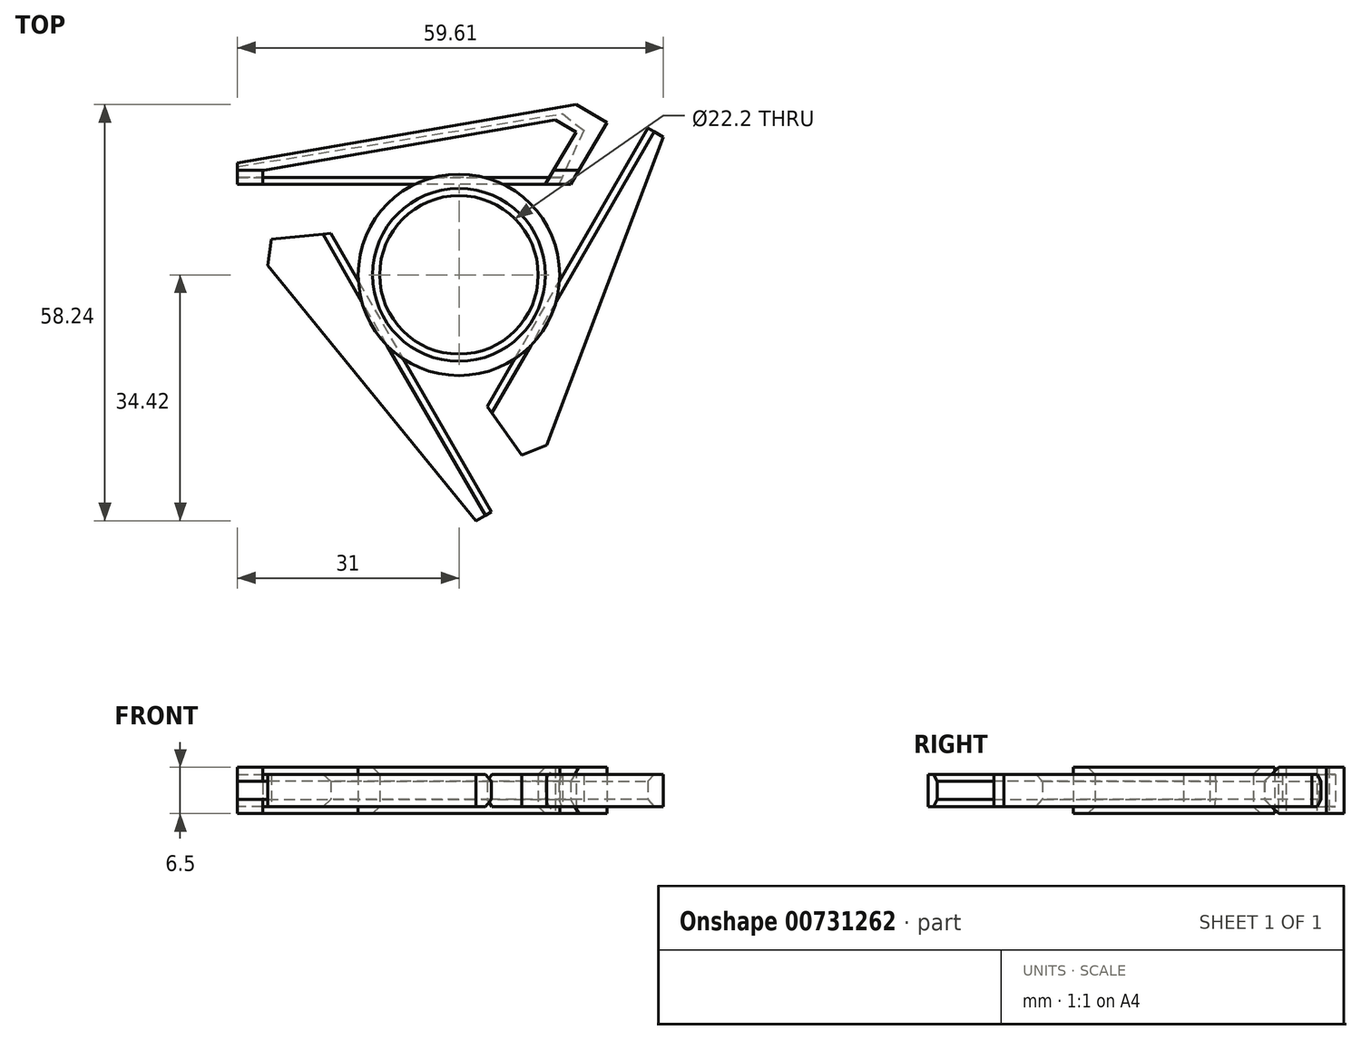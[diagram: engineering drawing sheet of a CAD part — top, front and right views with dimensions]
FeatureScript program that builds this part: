
annotation { "Feature Type Name" : "Feature", "Feature Type Description" : "" }
export const myFeature = defineFeature(function(context is Context, id is Id, definition is map)
    precondition{}
    {
        {
            var Q0;
            Q0=qCreatedBy(makeId("Top.planeOp"),FACE);
            var sketch = newSketch(context, id + "F0", { "sketchPlane" : qUnion([Q0])});
            skCircle(sketch, "E0", {"center": v(0, 0) * mm, "radius": 11.1 * mm});
            skCircle(sketch, "E1.0", {"center": v(0, 0) * mm, "radius": 14.1 * mm});
            skSolve(sketch);
        }
        {
            var Q0;
            Q0=qSketchRegion(id+"F0",true);
            extrude(context, id + "F1", {"entities" : qUnion([Q0]), "depth" : 6.5 * mm, "offsetDistance" : 25 * mm});
        }
        {
            var Q0;
            Q0=qCreatedBy(makeId("Top.planeOp"),FACE);
            cPlane(context, id + "F2", {"entities" : qUnion([Q0]), "cplaneType" : CPlaneType.OFFSET, "offset" : 1 * mm, "width" : 150 * mm, "height" : 150 * mm});
        }
        {
            var Q0;
            Q0=qCreatedBy(id+"F2.planeOp",FACE);
            var sketch = newSketch(context, id + "F3", { "sketchPlane" : qUnion([Q0])});
            skLineSegment(sketch, "E2", {"start": v(0, 0) * mm, "end": v(0, 12.64) * mm});
            skLineSegment(sketch, "E3", {"start": v(0, 12.64) * mm, "end": v(14, 12.64) * mm});
            skLineSegment(sketch, "E4", {"start": v(14, 12.64) * mm, "end": v(14, 17.64) * mm});
            skLineSegment(sketch, "E5", {"start": v(14, 17.64) * mm, "end": v(-31, 17.64) * mm});
            skLineSegment(sketch, "E6.bottom", {"start": v(-31, 17.64) * mm, "end": v(0, 17.64) * mm});
            skLineSegment(sketch, "E6.top", {"start": v(-31, 12.64) * mm, "end": v(0, 12.64) * mm});
            skLineSegment(sketch, "E6.left", {"start": v(-31, 17.64) * mm, "end": v(-31, 12.64) * mm});
            skLineSegment(sketch, "E7", {"start": v(-31, 15.14) * mm, "end": v(14.5, 22.55) * mm});
            skLineSegment(sketch, "E8", {"start": v(14.5, 22.55) * mm, "end": v(17.46, 20.2) * mm});
            skLineSegment(sketch, "E9", {"start": v(17.46, 20.2) * mm, "end": v(14, 12.64) * mm});
            skLineSegment(sketch, "E10", {"start": v(-3.72, 12.64) * mm, "end": v(-10.56, 6.96) * mm});
            skLineSegment(sketch, "E11", {"start": v(-10.56, 6.96) * mm, "end": v(-31, 12.64) * mm});
            skSolve(sketch);
        }
        {
            var Q0;
            Q0=makeQuery(id+"F3.imprint","IMPRINT",FACE,{"disambiguationData":[TD([[makeQuery(id+"F3.imprint","IMPRINT",EDGE,{"derivedFrom":sQuery(id+"F3.wireOp",EDGE,"E3")}),1.0]])]});
            var Q1;
            Q1=makeQuery(id+"F3.imprint","IMPRINT",FACE,{"disambiguationData":[TD([[makeQuery(id+"F3.imprint","IMPRINT",EDGE,{"derivedFrom":sQuery(id+"F3.wireOp",EDGE,"E4")}),-1.0]])]});
            extrude(context, id + "F4", {"entities" : qUnion([Q0, Q1]), "depth" : 4.5 * mm, "offsetDistance" : 25 * mm});
        }
        {
            var Q0;
            Q0=makeQuery(id+"F1.opExtrude","CAP_EDGE",EDGE,{"disambiguationData":[OSD([sQuery(id+"F0.wireOp",EDGE,"E0")])],"isStart":false});
            var Q1;
            Q1=makeQuery(id+"F1.opExtrude","SWEPT_FACE",FACE,{"disambiguationData":[OSD([sQuery(id+"F0.wireOp",EDGE,"E0")])]});
            chamfer(context, id + "F5", {"entities" : qUnion([Q0, Q1]), "width" : 1 * mm, "tangentPropagation" : true});
        }
        {
            var Q0;
            Q0=qCreatedBy(makeId("Top.planeOp"),FACE);
            var sketch = newSketch(context, id + "F6", { "sketchPlane" : qUnion([Q0])});
            skLineSegment(sketch, "E12", {"start": v(0, 0) * mm, "end": v(0, 12.66) * mm});
            skLineSegment(sketch, "E13", {"start": v(0, 12.66) * mm, "end": v(15.66, 12.66) * mm});
            skLineSegment(sketch, "E14", {"start": v(15.66, 12.66) * mm, "end": v(20.71, 21.3) * mm});
            skLineSegment(sketch, "E15", {"start": v(20.71, 21.3) * mm, "end": v(16.4, 23.82) * mm});
            skLineSegment(sketch, "E16", {"start": v(0, 12.66) * mm, "end": v(-31, 12.66) * mm});
            skLineSegment(sketch, "E17", {"start": v(-31, 12.66) * mm, "end": v(-31, 15.65) * mm});
            skLineSegment(sketch, "E18", {"start": v(-31, 15.65) * mm, "end": v(16.4, 23.82) * mm});
            skLineSegment(sketch, "E19", {"start": v(-27.48, 12.66) * mm, "end": v(-27.48, 14.6) * mm});
            skLineSegment(sketch, "E20", {"start": v(-27.48, 14.6) * mm, "end": v(13.5, 21.66) * mm});
            skLineSegment(sketch, "E21", {"start": v(13.5, 21.66) * mm, "end": v(16.4, 19.97) * mm});
            skLineSegment(sketch, "E22", {"start": v(16.4, 19.97) * mm, "end": v(12.12, 12.66) * mm});
            skSolve(sketch);
        }
        {
            var Q0;
            {var subQ3=sQuery(id+"F6.wireOp",EDGE,"E14");Q0=makeQuery(id+"F6.imprint","IMPRINT",FACE,{"disambiguationData":[TD([[makeQuery(id+"F6.imprint","IMPRINT",EDGE,{"derivedFrom":subQ3}),1.0]])]});}
            extrude(context, id + "F7", {"entities" : qUnion([Q0]), "depth" : 6.5 * mm, "offsetDistance" : 25 * mm});
        }
        {
            var Q0;
            Q0=makeQuery(id+"F4.opExtrude","CAP_EDGE",EDGE,{"disambiguationData":[OSD([sQuery(id+"F3.wireOp",EDGE,"E3"),sQuery(id+"F3.wireOp",EDGE,"E6.top")])],"isStart":false});
            var Q1;
            Q1=makeQuery(id+"F4.opExtrude","CAP_EDGE",EDGE,{"disambiguationData":[OSD([sQuery(id+"F3.wireOp",EDGE,"E3"),sQuery(id+"F3.wireOp",EDGE,"E6.top")])],"isStart":true});
            chamfer(context, id + "F8", {"entities" : qUnion([Q0, Q1]), "width" : 1 * mm, "tangentPropagation" : true});
        }
        {
            var Q0;
            Q0=makeQuery(id+"F7.opExtrude","CAP_EDGE",EDGE,{"disambiguationData":[OSD([sQuery(id+"F6.wireOp",EDGE,"E16")])],"isStart":false});
            var Q1;
            Q1=makeQuery(id+"F7.opExtrude","CAP_EDGE",EDGE,{"disambiguationData":[OSD([sQuery(id+"F6.wireOp",EDGE,"E13")])],"isStart":false});
            var Q2;
            Q2=makeQuery(id+"F7.opExtrude","CAP_EDGE",EDGE,{"disambiguationData":[OSD([sQuery(id+"F6.wireOp",EDGE,"E16")])],"isStart":true});
            var Q3;
            Q3=makeQuery(id+"F7.opExtrude","CAP_EDGE",EDGE,{"disambiguationData":[OSD([sQuery(id+"F6.wireOp",EDGE,"E13")])],"isStart":true});
            chamfer(context, id + "F9", {"entities" : qUnion([Q0, Q1, Q2, Q3]), "width" : 1.97 * mm, "tangentPropagation" : true});
        }
        {
            var Q0;
            Q0=makeQuery(id+"F4.opExtrude","SWEPT_BODY",BODY,{"disambiguationData":[OSD([sQuery(id+"F3.wireOp",EDGE,"E3"),sQuery(id+"F3.wireOp",EDGE,"E4"),sQuery(id+"F3.wireOp",EDGE,"E5"),sQuery(id+"F3.wireOp",EDGE,"E6.bottom"),sQuery(id+"F3.wireOp",EDGE,"E6.top"),sQuery(id+"F3.wireOp",EDGE,"E6.left")])]});
            var Q1;
            Q1=makeQuery(id+"F1.opExtrude","SWEPT_FACE",FACE,{"disambiguationData":[OSD([sQuery(id+"F0.wireOp",EDGE,"E1.0")])]});
            circularPattern(context, id + "F10", {"entities" : qUnion([Q0]), "axis" : qUnion([Q1]), "angle" : 360 * degree, "instanceCount" : 3, "equalSpace" : true});
        }
    });
